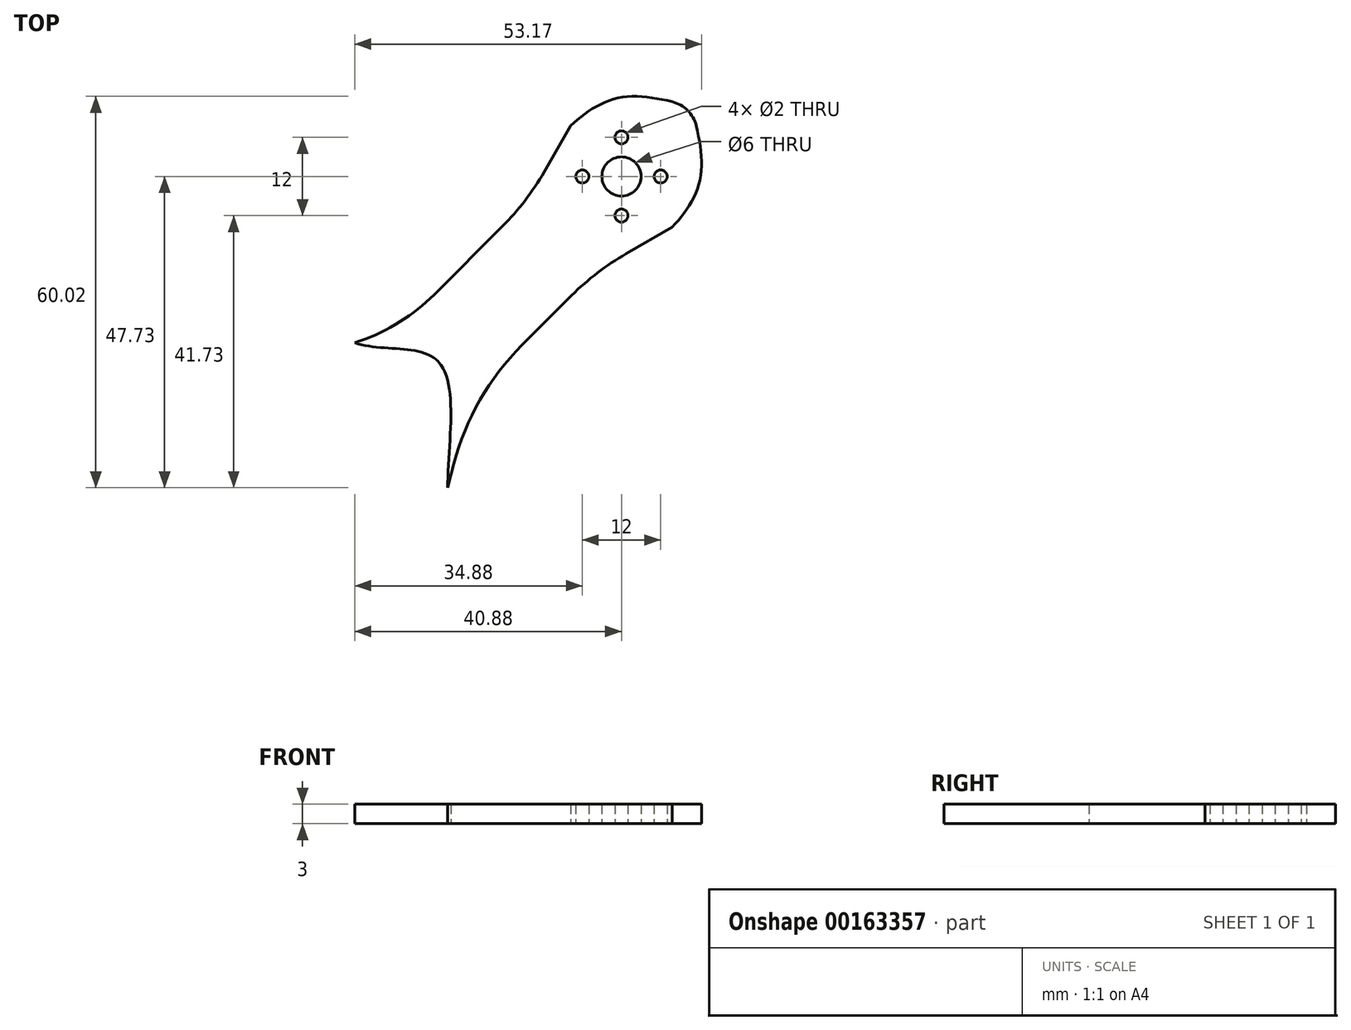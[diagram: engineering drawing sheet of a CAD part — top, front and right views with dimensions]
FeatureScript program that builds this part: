
annotation { "Feature Type Name" : "Feature", "Feature Type Description" : "" }
export const myFeature = defineFeature(function(context is Context, id is Id, definition is map)
    precondition{}
    {
        {
            var Q0;
            Q0=qCreatedBy(makeId("Top.planeOp"),FACE);
            var sketch = newSketch(context, id + "F0", { "sketchPlane" : qUnion([Q0])});
            skLineSegment(sketch, "E0.bottom", {"start": v(18, 18) * mm, "end": v(-18, 18) * mm, "construction": true});
            skLineSegment(sketch, "E0.top", {"start": v(18, -18) * mm, "end": v(-18, -18) * mm, "construction": true});
            skLineSegment(sketch, "E0.left", {"start": v(18, 18) * mm, "end": v(18, -18) * mm, "construction": true});
            skLineSegment(sketch, "E0.right", {"start": v(-18, 18) * mm, "end": v(-18, -18) * mm, "construction": true});
            skPoint(sketch, "E0.middle", {"position": v(0, 0) * mm});
            skLineSegment(sketch, "E1.bottom", {"start": v(15.25, 15.25) * mm, "end": v(-15.25, 15.25) * mm, "construction": true});
            skLineSegment(sketch, "E1.top", {"start": v(15.25, -15.25) * mm, "end": v(-15.25, -15.25) * mm, "construction": true});
            skLineSegment(sketch, "E1.left", {"start": v(15.25, 15.25) * mm, "end": v(15.25, -15.25) * mm, "construction": true});
            skLineSegment(sketch, "E1.right", {"start": v(-15.25, 15.25) * mm, "end": v(-15.25, -15.25) * mm, "construction": true});
            skCircle(sketch, "E2", {"center": v(15.25, 15.25) * mm, "radius": 1.5 * mm});
            skCircle(sketch, "E3", {"center": v(15.25, -15.25) * mm, "radius": 1.5 * mm});
            skCircle(sketch, "E4", {"center": v(-15.25, -15.25) * mm, "radius": 1.5 * mm});
            skCircle(sketch, "E5", {"center": v(-15.25, 15.25) * mm, "radius": 1.5 * mm});
            skLineSegment(sketch, "E6", {"start": v(-47.73, -47.73) * mm, "end": v(0, 0) * mm, "construction": true});
            skLineSegment(sketch, "E7", {"start": v(0, 0) * mm, "end": v(47.73, 47.73) * mm, "construction": true});
            skLineSegment(sketch, "E8", {"start": v(0, 44.74) * mm, "end": v(0, -45.9) * mm, "construction": true});
            skLineSegment(sketch, "E9", {"start": v(-44.2, 0) * mm, "end": v(46.03, 0) * mm, "construction": true});
            skLineSegment(sketch, "E10.MirrorCS", {"start": v(47.73, -47.73) * mm, "end": v(0, 0) * mm, "construction": true});
            skLineSegment(sketch, "E11.MirrorCS", {"start": v(0, 0) * mm, "end": v(-47.73, 47.73) * mm, "construction": true});
            skCircle(sketch, "E12", {"center": v(47.73, 47.73) * mm, "radius": 9 * mm, "construction": true});
            skCircle(sketch, "E13", {"center": v(47.73, 47.73) * mm, "radius": 6 * mm, "construction": true});
            skCircle(sketch, "E14", {"center": v(47.73, 47.73) * mm, "radius": 3 * mm});
            skLineSegment(sketch, "E15", {"start": v(47.73, 47.73) * mm, "end": v(47.73, 56.73) * mm, "construction": true});
            skLineSegment(sketch, "E16", {"start": v(47.73, 56.73) * mm, "end": v(47.73, 47.73) * mm, "construction": true});
            skLineSegment(sketch, "E17", {"start": v(47.73, 38.73) * mm, "end": v(47.73, 47.73) * mm, "construction": true});
            skLineSegment(sketch, "E18", {"start": v(47.73, 47.73) * mm, "end": v(56.73, 47.73) * mm, "construction": true});
            skLineSegment(sketch, "E19", {"start": v(38.73, 47.73) * mm, "end": v(47.73, 47.73) * mm, "construction": true});
            skCircle(sketch, "E20", {"center": v(47.73, 53.73) * mm, "radius": 1 * mm});
            skCircle(sketch, "E21", {"center": v(53.73, 47.73) * mm, "radius": 1 * mm});
            skCircle(sketch, "E22", {"center": v(47.73, 41.73) * mm, "radius": 1 * mm});
            skCircle(sketch, "E23", {"center": v(41.73, 47.73) * mm, "radius": 1 * mm});
            skCircle(sketch, "E24.MirrorC", {"center": v(-47.73, 47.73) * mm, "radius": 9 * mm, "construction": true});
            skCircle(sketch, "E25.MirrorC", {"center": v(-47.73, 47.73) * mm, "radius": 6 * mm, "construction": true});
            skCircle(sketch, "E26.MirrorC", {"center": v(-47.73, 41.73) * mm, "radius": 1 * mm, "construction": true});
            skCircle(sketch, "E27.MirrorC", {"center": v(-47.73, 41.73) * mm, "radius": 1 * mm});
            skLineSegment(sketch, "E28.MirrorCS", {"start": v(-47.73, 38.73) * mm, "end": v(-47.73, 47.73) * mm, "construction": true});
            skCircle(sketch, "E29.MirrorC", {"center": v(-47.73, 47.73) * mm, "radius": 3 * mm, "construction": true});
            skCircle(sketch, "E30.MirrorC", {"center": v(-47.73, 47.73) * mm, "radius": 3 * mm});
            skLineSegment(sketch, "E31.MirrorCS", {"start": v(-47.73, 47.73) * mm, "end": v(-56.73, 47.73) * mm, "construction": true});
            skCircle(sketch, "E32.MirrorC", {"center": v(-53.73, 47.73) * mm, "radius": 1 * mm, "construction": true});
            skCircle(sketch, "E33.MirrorC", {"center": v(-53.73, 47.73) * mm, "radius": 1 * mm});
            skCircle(sketch, "E34.MirrorC", {"center": v(-47.73, 53.73) * mm, "radius": 1 * mm, "construction": true});
            skCircle(sketch, "E35.MirrorC", {"center": v(-47.73, 53.73) * mm, "radius": 1 * mm});
            skLineSegment(sketch, "E36.MirrorCS", {"start": v(-47.73, 56.73) * mm, "end": v(-47.73, 47.73) * mm, "construction": true});
            skCircle(sketch, "E37.MirrorC", {"center": v(-41.73, 47.73) * mm, "radius": 1 * mm, "construction": true});
            skCircle(sketch, "E38.MirrorC", {"center": v(-41.73, 47.73) * mm, "radius": 1 * mm});
            skLineSegment(sketch, "E39.MirrorCS", {"start": v(-38.73, 47.73) * mm, "end": v(-47.73, 47.73) * mm, "construction": true});
            skCircle(sketch, "E40.MirrorC", {"center": v(47.73, -47.73) * mm, "radius": 9 * mm, "construction": true});
            skCircle(sketch, "E41.MirrorC", {"center": v(47.73, -47.73) * mm, "radius": 6 * mm, "construction": true});
            skCircle(sketch, "E42.MirrorC", {"center": v(53.73, -47.73) * mm, "radius": 1 * mm, "construction": true});
            skCircle(sketch, "E43.MirrorC", {"center": v(53.73, -47.73) * mm, "radius": 1 * mm});
            skLineSegment(sketch, "E44.MirrorCS", {"start": v(47.73, -47.73) * mm, "end": v(56.73, -47.73) * mm, "construction": true});
            skCircle(sketch, "E45.MirrorC", {"center": v(47.73, -47.73) * mm, "radius": 3 * mm, "construction": true});
            skCircle(sketch, "E46.MirrorC", {"center": v(47.73, -47.73) * mm, "radius": 3 * mm});
            skLineSegment(sketch, "E47.MirrorCS", {"start": v(47.73, -38.73) * mm, "end": v(47.73, -47.73) * mm, "construction": true});
            skLineSegment(sketch, "E48.MirrorCS", {"start": v(38.73, -47.73) * mm, "end": v(47.73, -47.73) * mm, "construction": true});
            skCircle(sketch, "E49.MirrorC", {"center": v(41.73, -47.73) * mm, "radius": 1 * mm, "construction": true});
            skCircle(sketch, "E50.MirrorC", {"center": v(41.73, -47.73) * mm, "radius": 1 * mm});
            skCircle(sketch, "E51.MirrorC", {"center": v(47.73, -53.73) * mm, "radius": 1 * mm, "construction": true});
            skCircle(sketch, "E52.MirrorC", {"center": v(47.73, -53.73) * mm, "radius": 1 * mm});
            skLineSegment(sketch, "E53.MirrorCS", {"start": v(47.73, -56.73) * mm, "end": v(47.73, -47.73) * mm, "construction": true});
            skCircle(sketch, "E54.MirrorC", {"center": v(47.73, -41.73) * mm, "radius": 1 * mm, "construction": true});
            skCircle(sketch, "E55.MirrorC", {"center": v(47.73, -41.73) * mm, "radius": 1 * mm});
            skCircle(sketch, "E56.MirrorC", {"center": v(-47.73, -47.73) * mm, "radius": 9 * mm, "construction": true});
            skCircle(sketch, "E57.MirrorC", {"center": v(-41.73, -47.73) * mm, "radius": 1 * mm, "construction": true});
            skCircle(sketch, "E58.MirrorC", {"center": v(-41.73, -47.73) * mm, "radius": 1 * mm});
            skLineSegment(sketch, "E59.MirrorCS", {"start": v(-38.73, -47.73) * mm, "end": v(-47.73, -47.73) * mm, "construction": true});
            skCircle(sketch, "E60.MirrorC", {"center": v(-47.73, -47.73) * mm, "radius": 6 * mm, "construction": true});
            skCircle(sketch, "E61.MirrorC", {"center": v(-47.73, -41.73) * mm, "radius": 1 * mm, "construction": true});
            skCircle(sketch, "E62.MirrorC", {"center": v(-47.73, -41.73) * mm, "radius": 1 * mm});
            skLineSegment(sketch, "E63.MirrorCS", {"start": v(-47.73, -47.73) * mm, "end": v(-56.73, -47.73) * mm, "construction": true});
            skCircle(sketch, "E64.MirrorC", {"center": v(-53.73, -47.73) * mm, "radius": 1 * mm, "construction": true});
            skCircle(sketch, "E65.MirrorC", {"center": v(-53.73, -47.73) * mm, "radius": 1 * mm});
            skCircle(sketch, "E66.MirrorC", {"center": v(-47.73, -53.73) * mm, "radius": 1 * mm, "construction": true});
            skCircle(sketch, "E67.MirrorC", {"center": v(-47.73, -53.73) * mm, "radius": 1 * mm});
            skLineSegment(sketch, "E68.MirrorCS", {"start": v(-47.73, -56.73) * mm, "end": v(-47.73, -47.73) * mm, "construction": true});
            skLineSegment(sketch, "E69.MirrorCS", {"start": v(-47.73, -38.73) * mm, "end": v(-47.73, -47.73) * mm, "construction": true});
            skLineSegment(sketch, "E70.bottom", {"start": v(19.5, 19.5) * mm, "end": v(-19.5, 19.5) * mm, "construction": true});
            skLineSegment(sketch, "E70.top", {"start": v(19.5, -19.5) * mm, "end": v(-19.5, -19.5) * mm, "construction": true});
            skLineSegment(sketch, "E70.left", {"start": v(19.5, 19.5) * mm, "end": v(19.5, -19.5) * mm, "construction": true});
            skLineSegment(sketch, "E70.right", {"start": v(-19.5, 19.5) * mm, "end": v(-19.5, -19.5) * mm, "construction": true});
            skFitSpline(sketch, "E71", {"points": [v(-19.5, 19.5) * mm, v(-6.87, 22.22) * mm, v(0, 25.99) * mm, v(6.85, 22.22) * mm, v(19.5, 19.5) * mm, v(21.07, 0) * mm, v(19.5, -19.5) * mm, v(0, -34) * mm, v(-19.5, -19.5) * mm, v(-21.07, 0) * mm, v(-19.5, 19.5) * mm]});
            skCircle(sketch, "E72.cCircle", {"center": v(0, 22.21) * mm, "radius": 2.75 * mm, "construction": true});
            skLineSegment(sketch, "E72.0", {"start": v(2.68, 22.82) * mm, "end": v(1.87, 20.2) * mm, "construction": true});
            skLineSegment(sketch, "E72.1", {"start": v(1.87, 20.2) * mm, "end": v(-0.81, 19.58) * mm, "construction": true});
            skLineSegment(sketch, "E72.2", {"start": v(-0.81, 19.58) * mm, "end": v(-2.68, 21.6) * mm, "construction": true});
            skLineSegment(sketch, "E72.3", {"start": v(-2.68, 21.6) * mm, "end": v(-1.87, 24.23) * mm, "construction": true});
            skLineSegment(sketch, "E72.4", {"start": v(-1.87, 24.23) * mm, "end": v(0.81, 24.84) * mm, "construction": true});
            skLineSegment(sketch, "E72.5", {"start": v(0.81, 24.84) * mm, "end": v(2.68, 22.82) * mm, "construction": true});
            skCircle(sketch, "E73.cCircle", {"center": v(0, -30.03) * mm, "radius": 2.75 * mm, "construction": true});
            skLineSegment(sketch, "E73.0", {"start": v(2.68, -29.42) * mm, "end": v(1.87, -32.05) * mm, "construction": true});
            skLineSegment(sketch, "E73.1", {"start": v(1.87, -32.05) * mm, "end": v(-0.81, -32.65) * mm, "construction": true});
            skLineSegment(sketch, "E73.2", {"start": v(-0.81, -32.65) * mm, "end": v(-2.68, -30.63) * mm, "construction": true});
            skLineSegment(sketch, "E73.3", {"start": v(-2.68, -30.63) * mm, "end": v(-1.87, -28) * mm, "construction": true});
            skLineSegment(sketch, "E73.4", {"start": v(-1.87, -28) * mm, "end": v(0.81, -27.4) * mm, "construction": true});
            skLineSegment(sketch, "E73.5", {"start": v(0.81, -27.4) * mm, "end": v(2.68, -29.42) * mm, "construction": true});
            skPoint(sketch, "E74", {"position": v(0, 19.5) * mm});
            skLineSegment(sketch, "E75", {"start": v(-6.87, 22.22) * mm, "end": v(6.85, 22.22) * mm, "construction": true});
            skLineSegment(sketch, "E76", {"start": v(55.5, 39.95) * mm, "end": v(55.5, 39.95) * mm});
            skLineSegment(sketch, "E77", {"start": v(33.23, 43.84) * mm, "end": v(38.54, 38.54) * mm, "construction": true});
            skLineSegment(sketch, "E78", {"start": v(38.54, 38.54) * mm, "end": v(43.84, 33.23) * mm, "construction": true});
            skLineSegment(sketch, "E79", {"start": v(39.95, 55.5) * mm, "end": v(47.73, 47.73) * mm, "construction": true});
            skLineSegment(sketch, "E80", {"start": v(47.73, 47.73) * mm, "end": v(55.5, 39.95) * mm, "construction": true});
            skLineSegment(sketch, "E81", {"start": v(39.95, 55.5) * mm, "end": v(35.87, 48.43) * mm});
            skLineSegment(sketch, "E82", {"start": v(55.5, 39.95) * mm, "end": v(48.43, 35.87) * mm});
            skLineSegment(sketch, "E83", {"start": v(14.2, 24.8) * mm, "end": v(19.5, 19.5) * mm, "construction": true});
            skLineSegment(sketch, "E84", {"start": v(19.5, 19.5) * mm, "end": v(24.8, 14.2) * mm, "construction": true});
            skLineSegment(sketch, "E85", {"start": v(29.5, 40.1) * mm, "end": v(19.03, 29.64) * mm});
            skLineSegment(sketch, "E86", {"start": v(40.1, 29.5) * mm, "end": v(32.46, 21.85) * mm});
            skLineSegment(sketch, "E87", {"start": v(22.05, 3.73) * mm, "end": v(21.07, 0) * mm});
            skLineSegment(sketch, "E88", {"start": v(7.75, 22.54) * mm, "end": v(6.85, 22.22) * mm});
            skPoint(sketch, "E89.visualSharp", {"position": v(24.8, 14.2) * mm});
            skArc(sketch, "E89.filletArc", {"start": v(32.46, 21.85) * mm, "mid": v(26.05, 13.48) * mm, "end": v(22.05, 3.73) * mm});
            skPoint(sketch, "E90.visualSharp", {"position": v(14.2, 24.8) * mm});
            skArc(sketch, "E90.filletArc", {"start": v(7.75, 22.54) * mm, "mid": v(13.79, 25.45) * mm, "end": v(19.03, 29.64) * mm});
            skPoint(sketch, "E91.visualSharp", {"position": v(33.23, 43.84) * mm});
            skArc(sketch, "E91.filletArc", {"start": v(29.5, 40.1) * mm, "mid": v(32.96, 44.05) * mm, "end": v(35.87, 48.43) * mm});
            skPoint(sketch, "E92.visualSharp", {"position": v(43.84, 33.23) * mm});
            skArc(sketch, "E92.filletArc", {"start": v(48.43, 35.87) * mm, "mid": v(44.05, 32.96) * mm, "end": v(40.1, 29.5) * mm});
            skLineSegment(sketch, "E93.MirrorCS", {"start": v(-7.75, 22.54) * mm, "end": v(-6.85, 22.22) * mm});
            skArc(sketch, "E94.MirrorCS", {"start": v(-7.75, 22.54) * mm, "mid": v(-13.79, 25.45) * mm, "end": v(-19.03, 29.64) * mm});
            skLineSegment(sketch, "E95.MirrorCS", {"start": v(-29.5, 40.1) * mm, "end": v(-19.03, 29.64) * mm});
            skArc(sketch, "E96.MirrorCS", {"start": v(-29.5, 40.1) * mm, "mid": v(-32.96, 44.05) * mm, "end": v(-35.87, 48.43) * mm});
            skLineSegment(sketch, "E97.MirrorCS", {"start": v(-39.95, 55.5) * mm, "end": v(-35.87, 48.43) * mm});
            skLineSegment(sketch, "E98.MirrorCS", {"start": v(-55.5, 39.95) * mm, "end": v(-55.5, 39.95) * mm});
            skLineSegment(sketch, "E99.MirrorCS", {"start": v(-55.5, 39.95) * mm, "end": v(-48.43, 35.87) * mm});
            skArc(sketch, "E100.MirrorCS", {"start": v(-48.43, 35.87) * mm, "mid": v(-44.05, 32.96) * mm, "end": v(-40.1, 29.5) * mm});
            skLineSegment(sketch, "E101.MirrorCS", {"start": v(-40.1, 29.5) * mm, "end": v(-32.46, 21.85) * mm});
            skArc(sketch, "E102.MirrorCS", {"start": v(-32.46, 21.85) * mm, "mid": v(-26.05, 13.48) * mm, "end": v(-22.05, 3.73) * mm});
            skLineSegment(sketch, "E103.MirrorCS", {"start": v(-22.05, 3.73) * mm, "end": v(-21.07, 0) * mm});
            skLineSegment(sketch, "E104.MirrorCS", {"start": v(14.2, -24.8) * mm, "end": v(19.5, -19.5) * mm, "construction": true});
            skLineSegment(sketch, "E105.MirrorCS", {"start": v(19.5, -19.5) * mm, "end": v(24.8, -14.2) * mm, "construction": true});
            skLineSegment(sketch, "E106.MirrorCS", {"start": v(33.23, -43.84) * mm, "end": v(38.54, -38.54) * mm, "construction": true});
            skLineSegment(sketch, "E107.MirrorCS", {"start": v(38.54, -38.54) * mm, "end": v(43.84, -33.23) * mm, "construction": true});
            skLineSegment(sketch, "E108.MirrorCS", {"start": v(55.5, -39.95) * mm, "end": v(55.5, -39.95) * mm});
            skLineSegment(sketch, "E109.MirrorCS", {"start": v(55.5, -39.95) * mm, "end": v(48.43, -35.87) * mm});
            skLineSegment(sketch, "E110.MirrorCS", {"start": v(39.95, -55.5) * mm, "end": v(35.87, -48.43) * mm});
            skArc(sketch, "E111.MirrorCS", {"start": v(48.43, -35.87) * mm, "mid": v(44.05, -32.96) * mm, "end": v(40.1, -29.5) * mm});
            skArc(sketch, "E112.MirrorCS", {"start": v(29.5, -40.1) * mm, "mid": v(32.96, -44.05) * mm, "end": v(35.87, -48.43) * mm});
            skLineSegment(sketch, "E113", {"start": v(40.1, -29.5) * mm, "end": v(32.46, -21.85) * mm});
            skLineSegment(sketch, "E114", {"start": v(22.05, -3.73) * mm, "end": v(21.07, 0) * mm});
            skLineSegment(sketch, "E115", {"start": v(29.5, -40.1) * mm, "end": v(20.34, -30.95) * mm});
            skPoint(sketch, "E116", {"position": v(0, -19.5) * mm});
            skPoint(sketch, "E117.visualSharp", {"position": v(14.2, -24.8) * mm});
            skArc(sketch, "E117.filletArc", {"start": v(20.34, -30.95) * mm, "mid": v(17.71, -28.54) * mm, "end": v(14.88, -26.38) * mm});
            skPoint(sketch, "E118.visualSharp", {"position": v(24.8, -14.2) * mm});
            skArc(sketch, "E118.filletArc", {"start": v(22.05, -3.73) * mm, "mid": v(26.05, -13.48) * mm, "end": v(32.46, -21.85) * mm});
            skArc(sketch, "E119.MirrorCS", {"start": v(-20.34, -30.95) * mm, "mid": v(-17.71, -28.54) * mm, "end": v(-14.88, -26.38) * mm});
            skLineSegment(sketch, "E120.MirrorCS", {"start": v(-29.5, -40.1) * mm, "end": v(-20.34, -30.95) * mm});
            skArc(sketch, "E121.MirrorCS", {"start": v(-29.5, -40.1) * mm, "mid": v(-32.96, -44.05) * mm, "end": v(-35.87, -48.43) * mm});
            skLineSegment(sketch, "E122.MirrorCS", {"start": v(-39.95, -55.5) * mm, "end": v(-35.87, -48.43) * mm});
            skArc(sketch, "E123.MirrorCS", {"start": v(-55.5, -39.95) * mm, "mid": v(-55.9, -40.36) * mm, "end": v(-56.26, -40.8) * mm});
            skLineSegment(sketch, "E124.MirrorCS", {"start": v(-55.5, -39.95) * mm, "end": v(-48.43, -35.87) * mm});
            skArc(sketch, "E125.MirrorCS", {"start": v(-48.43, -35.87) * mm, "mid": v(-44.05, -32.96) * mm, "end": v(-40.1, -29.5) * mm});
            skLineSegment(sketch, "E126.MirrorCS", {"start": v(-40.1, -29.5) * mm, "end": v(-32.46, -21.85) * mm});
            skArc(sketch, "E127.MirrorCS", {"start": v(-22.05, -3.73) * mm, "mid": v(-26.05, -13.48) * mm, "end": v(-32.46, -21.85) * mm});
            skLineSegment(sketch, "E128.MirrorCS", {"start": v(-22.05, -3.73) * mm, "end": v(-21.07, 0) * mm});
            skFitSpline(sketch, "E129.trimOffspring", {"points": [v(-19.5, 19.5) * mm, v(-6.87, 22.22) * mm, v(0, 26) * mm, v(6.85, 22.22) * mm, v(19.5, 19.5) * mm, v(21.07, 0) * mm, v(19.5, -19.5) * mm, v(0, -34) * mm, v(-19.5, -19.5) * mm, v(-21.07, 0) * mm, v(-19.5, 19.5) * mm]});
            skPoint(sketch, "E130.orphan", {"position": v(-6.06, -21.76) * mm});
            skPoint(sketch, "E131.orphan", {"position": v(6.06, -21.76) * mm});
            skFitSpline(sketch, "E132.trimOffspring", {"points": [v(-19.5, 19.5) * mm, v(-6.87, 22.22) * mm, v(0, 26) * mm, v(6.85, 22.22) * mm, v(19.5, 19.5) * mm, v(21.07, 0) * mm, v(19.5, -19.5) * mm, v(0, -34) * mm, v(-19.5, -19.5) * mm, v(-21.07, 0) * mm, v(-19.5, 19.5) * mm]});
            skCircle(sketch, "E133.MirrorC", {"center": v(-47.73, -47.73) * mm, "radius": 3 * mm});
            skLineSegment(sketch, "E134.bottom", {"start": v(10.5, 10) * mm, "end": v(13.5, 10) * mm});
            skLineSegment(sketch, "E134.top", {"start": v(10.5, -10) * mm, "end": v(13.5, -10) * mm});
            skLineSegment(sketch, "E134.left", {"start": v(10.5, 10) * mm, "end": v(10.5, -10) * mm});
            skLineSegment(sketch, "E134.right", {"start": v(13.5, 10) * mm, "end": v(13.5, -10) * mm});
            skPoint(sketch, "E134.middle", {"position": v(12, 0) * mm});
            skLineSegment(sketch, "E135.MirrorCS", {"start": v(-10.5, 10) * mm, "end": v(-13.5, 10) * mm});
            skLineSegment(sketch, "E136.MirrorCS", {"start": v(-13.5, 10) * mm, "end": v(-13.5, -10) * mm});
            skLineSegment(sketch, "E137.MirrorCS", {"start": v(-10.5, 10) * mm, "end": v(-10.5, -10) * mm});
            skLineSegment(sketch, "E138.MirrorCS", {"start": v(-10.5, -10) * mm, "end": v(-13.5, -10) * mm});
            skCircle(sketch, "E139", {"center": v(0, 22.21) * mm, "radius": 1.5 * mm});
            skCircle(sketch, "E140", {"center": v(0, -30.03) * mm, "radius": 1.5 * mm});
            skLineSegment(sketch, "E141", {"start": v(47.73, 47.73) * mm, "end": v(58.43, 58.43) * mm, "construction": true});
            skLineSegment(sketch, "E142", {"start": v(47.73, 56.73) * mm, "end": v(47.73, 59.86) * mm, "construction": true});
            skFitSpline(sketch, "E143", {"points": [v(39.95, 55.5) * mm, v(47.73, 59.86) * mm, v(58.43, 58.43) * mm, v(67.08, 55.96) * mm], "startDerivative": vector(19.86, 18.67) * mm, "endDerivative": vector(24.91, -8.05) * mm});
            skLineSegment(sketch, "E144.trimOffspring", {"start": v(39.95, 55.5) * mm, "end": v(39.95, 55.5) * mm});
            skFitSpline(sketch, "E145.MirrorCS", {"points": [v(55.5, 39.95) * mm, v(59.86, 47.73) * mm, v(58.43, 58.43) * mm, v(55.96, 67.08) * mm], "startDerivative": vector(18.67, 19.86) * mm, "endDerivative": vector(-8.05, 24.91) * mm});
            skFitSpline(sketch, "E146.MirrorCS", {"points": [v(-39.95, 55.5) * mm, v(-47.73, 59.86) * mm, v(-58.43, 58.43) * mm, v(-67.08, 55.96) * mm], "startDerivative": vector(-19.86, 18.67) * mm, "endDerivative": vector(-24.91, -8.05) * mm});
            skFitSpline(sketch, "E147.MirrorCS", {"points": [v(-55.5, 39.95) * mm, v(-59.86, 47.73) * mm, v(-58.43, 58.43) * mm, v(-55.96, 67.08) * mm], "startDerivative": vector(-18.67, 19.86) * mm, "endDerivative": vector(8.05, 24.91) * mm});
            skFitSpline(sketch, "E148.MirrorCS", {"points": [v(39.95, -55.5) * mm, v(47.73, -59.86) * mm, v(58.43, -58.43) * mm, v(67.08, -55.96) * mm], "startDerivative": vector(19.86, -18.67) * mm, "endDerivative": vector(24.91, 8.05) * mm});
            skFitSpline(sketch, "E149.MirrorCS", {"points": [v(55.5, -39.95) * mm, v(59.86, -47.73) * mm, v(58.43, -58.43) * mm, v(55.96, -67.08) * mm], "startDerivative": vector(18.67, -19.86) * mm, "endDerivative": vector(-8.05, -24.91) * mm});
            skFitSpline(sketch, "E150.MirrorCS", {"points": [v(-55.5, -39.95) * mm, v(-59.86, -47.73) * mm, v(-58.43, -58.43) * mm, v(-55.96, -67.08) * mm], "startDerivative": vector(-18.67, -19.86) * mm, "endDerivative": vector(8.05, -24.91) * mm});
            skFitSpline(sketch, "E151.MirrorCS", {"points": [v(-39.95, -55.5) * mm, v(-47.73, -59.86) * mm, v(-58.43, -58.43) * mm, v(-67.08, -55.96) * mm], "startDerivative": vector(-19.86, -18.67) * mm, "endDerivative": vector(-24.91, 8.05) * mm});
            skLineSegment(sketch, "E152.trimOffspring", {"start": v(39.95, -55.5) * mm, "end": v(39.95, -55.5) * mm});
            skArc(sketch, "E153.trimOffspring", {"start": v(-40.8, -56.27) * mm, "mid": v(-40.36, -55.9) * mm, "end": v(-39.95, -55.5) * mm});
            skLineSegment(sketch, "E154.trimOffspring", {"start": v(-39.95, 55.5) * mm, "end": v(-39.95, 55.5) * mm});
            skArc(sketch, "E155.filletArc", {"start": v(59.19, 55.5) * mm, "mid": v(57.86, 57.86) * mm, "end": v(55.5, 59.19) * mm});
            skArc(sketch, "E156.filletArc", {"start": v(-55.5, 59.19) * mm, "mid": v(-57.86, 57.86) * mm, "end": v(-59.19, 55.5) * mm});
            skArc(sketch, "E157.filletArc", {"start": v(55.5, -59.19) * mm, "mid": v(57.86, -57.86) * mm, "end": v(59.19, -55.5) * mm});
            skArc(sketch, "E158.filletArc", {"start": v(-59.19, -55.5) * mm, "mid": v(-57.86, -57.86) * mm, "end": v(-55.5, -59.19) * mm});
            skLineSegment(sketch, "E159", {"start": v(0, -22.36) * mm, "end": v(3, -22.36) * mm, "construction": true});
            skLineSegment(sketch, "E160.left", {"start": v(3.77, -23.88) * mm, "end": v(3.77, -20.88) * mm});
            skLineSegment(sketch, "E160.right", {"start": v(2.23, -23.85) * mm, "end": v(2.23, -20.85) * mm});
            skPoint(sketch, "E160.middle", {"position": v(3, -22.36) * mm});
            skLineSegment(sketch, "E161.MirrorCS", {"start": v(-2.23, -23.85) * mm, "end": v(-2.23, -20.85) * mm});
            skLineSegment(sketch, "E162.MirrorCS", {"start": v(-3.77, -23.88) * mm, "end": v(-3.77, -20.88) * mm});
            skArc(sketch, "E163", {"start": v(2.23, -20.85) * mm, "mid": v(3.01, -20.08) * mm, "end": v(3.77, -20.88) * mm});
            skPoint(sketch, "E164.MirrorCS.end.orphan", {"position": v(-2.23, -23.85) * mm});
            skPoint(sketch, "E164.MirrorCS.start.orphan", {"position": v(-3.77, -23.88) * mm});
            skPoint(sketch, "E165.MirrorCS.end.orphan", {"position": v(-2.23, -20.85) * mm});
            skPoint(sketch, "E165.MirrorCS.start.orphan", {"position": v(-3.77, -20.88) * mm});
            skArc(sketch, "E166", {"start": v(2.23, -23.85) * mm, "mid": v(2.99, -24.62) * mm, "end": v(3.77, -23.88) * mm});
            skArc(sketch, "E167.MirrorCS", {"start": v(-2.23, -20.85) * mm, "mid": v(-3.01, -20.08) * mm, "end": v(-3.77, -20.88) * mm});
            skArc(sketch, "E168.MirrorCS", {"start": v(-2.23, -23.85) * mm, "mid": v(-2.99, -24.62) * mm, "end": v(-3.77, -23.88) * mm});
            skSolve(sketch);
        }
        {
            var Q0;
            Q0=qCreatedBy(makeId("Top.planeOp"),FACE);
            cPlane(context, id + "F1", {"entities" : qUnion([Q0]), "cplaneType" : CPlaneType.OFFSET, "offset" : 15 * mm, "width" : 150 * mm, "height" : 150 * mm});
        }
        {
            var Q0;
            Q0=qCreatedBy(id+"F1.planeOp",FACE);
            var sketch = newSketch(context, id + "F2", { "sketchPlane" : qUnion([Q0])});
            skLineSegment(sketch, "E169.bottom", {"start": v(17.96, 18.03) * mm, "end": v(-18.04, 18.03) * mm, "construction": true});
            skLineSegment(sketch, "E169.top", {"start": v(17.96, -17.97) * mm, "end": v(-18.04, -17.97) * mm, "construction": true});
            skLineSegment(sketch, "E169.left", {"start": v(17.96, 18.03) * mm, "end": v(17.96, -17.97) * mm, "construction": true});
            skLineSegment(sketch, "E169.right", {"start": v(-18.04, 18.03) * mm, "end": v(-18.04, -17.97) * mm, "construction": true});
            skPoint(sketch, "E169.middle", {"position": v(-0.04, 0.03) * mm});
            skLineSegment(sketch, "E170.bottom", {"start": v(15.2, 15.28) * mm, "end": v(-15.3, 15.28) * mm, "construction": true});
            skLineSegment(sketch, "E170.top", {"start": v(15.2, -15.22) * mm, "end": v(-15.3, -15.22) * mm, "construction": true});
            skLineSegment(sketch, "E170.left", {"start": v(15.2, 15.28) * mm, "end": v(15.2, -15.22) * mm, "construction": true});
            skLineSegment(sketch, "E170.right", {"start": v(-15.3, 15.28) * mm, "end": v(-15.3, -15.22) * mm, "construction": true});
            skCircle(sketch, "E171", {"center": v(15.2, 15.28) * mm, "radius": 1.5 * mm});
            skCircle(sketch, "E172", {"center": v(15.2, -15.22) * mm, "radius": 1.5 * mm});
            skCircle(sketch, "E173", {"center": v(-15.3, -15.22) * mm, "radius": 1.5 * mm});
            skCircle(sketch, "E174", {"center": v(-15.3, 15.28) * mm, "radius": 1.5 * mm});
            skLineSegment(sketch, "E175", {"start": v(-0.04, 44.77) * mm, "end": v(-0.04, -45.88) * mm, "construction": true});
            skLineSegment(sketch, "E176", {"start": v(-44.25, 0.03) * mm, "end": v(46, 0.03) * mm, "construction": true});
            skSolve(sketch);
        }
        {
            var Q0;
            Q0=qCreatedBy(makeId("Top.planeOp"),FACE);
            cPlane(context, id + "F3", {"entities" : qUnion([Q0]), "cplaneType" : CPlaneType.OFFSET, "offset" : 27 * mm, "width" : 150 * mm, "height" : 150 * mm});
        }
        {
            var Q0;
            Q0=qCreatedBy(makeId("Right.planeOp"),FACE);
            var sketch = newSketch(context, id + "F4", { "sketchPlane" : qUnion([Q0])});
            skLineSegment(sketch, "E177", {"start": v(1.3, 0) * mm, "end": v(1.3, 25) * mm, "construction": true});
            skLineSegment(sketch, "E178", {"start": v(1.3, 25) * mm, "end": v(-5.2, 36.26) * mm, "construction": true});
            skLineSegment(sketch, "E179", {"start": v(-5.2, 36.26) * mm, "end": v(5.2, 42.26) * mm, "construction": true});
            skLineSegment(sketch, "E180", {"start": v(5.2, 42.26) * mm, "end": v(18.2, 19.74) * mm, "construction": true});
            skLineSegment(sketch, "E181", {"start": v(18.2, 19.74) * mm, "end": v(7.8, 13.74) * mm, "construction": true});
            skLineSegment(sketch, "E182", {"start": v(7.8, 13.74) * mm, "end": v(1.3, 25) * mm, "construction": true});
            skLineSegment(sketch, "E183", {"start": v(5.2, 42.26) * mm, "end": v(22.17, 46.86) * mm, "construction": true});
            skLineSegment(sketch, "E184", {"start": v(22.17, 46.86) * mm, "end": v(30.67, 32.14) * mm, "construction": true});
            skLineSegment(sketch, "E185", {"start": v(30.67, 32.14) * mm, "end": v(18.2, 19.74) * mm, "construction": true});
            skLineSegment(sketch, "E186", {"start": v(1.3, 25) * mm, "end": v(26.42, 39.5) * mm, "construction": true});
            skLineSegment(sketch, "E187", {"start": v(18.2, 3.74) * mm, "end": v(4.77, 27) * mm, "construction": true});
            skLineSegment(sketch, "E188", {"start": v(4.77, 27) * mm, "end": v(3.2, 29.72) * mm, "construction": true});
            skSolve(sketch);
        }
        {
            var Q0;
            Q0=sQuery(id+"F4.wireOp",EDGE,"E184");
            var Q1;
            Q1=qCreatedBy(makeId("Top.planeOp"),FACE);
            cPlane(context, id + "F5", {"entities" : qUnion([Q0, Q1]), "cplaneType" : CPlaneType.LINE_ANGLE, "offset" : 25.4 * mm, "angle" : 0 * degree, "width" : 152.4 * mm, "height" : 152.4 * mm});
        }
        {
            var Q0;
            Q0=qCreatedBy(id+"F5.planeOp",FACE);
            cPlane(context, id + "F6", {"entities" : qUnion([Q0]), "cplaneType" : CPlaneType.OFFSET, "offset" : 0 * mm, "width" : 152.4 * mm, "height" : 152.4 * mm});
        }
        {
            var Q0;
            Q0=sQuery(id+"F0.wireOp",VERTEX,"E70.left.end");
            var Q1;
            Q1=sQuery(id+"F0.wireOp",EDGE,"E10.MirrorCS");
            cPlane(context, id + "F7", {"entities" : qUnion([Q0, Q1]), "cplaneType" : CPlaneType.LINE_POINT, "offset" : 25 * mm, "width" : 150 * mm, "height" : 150 * mm});
        }
        {
            var Q0;
            Q0=sQuery(id+"F0.wireOp",VERTEX,"E70.right.end");
            var Q1;
            Q1=sQuery(id+"F0.wireOp",EDGE,"E6");
            cPlane(context, id + "F8", {"entities" : qUnion([Q0, Q1]), "cplaneType" : CPlaneType.LINE_POINT, "offset" : 25 * mm, "width" : 150 * mm, "height" : 150 * mm});
        }
        {
            var Q0;
            Q0=sQuery(id+"F0.wireOp",VERTEX,"E70.right.start");
            var Q1;
            Q1=sQuery(id+"F0.wireOp",EDGE,"E11.MirrorCS");
            cPlane(context, id + "F9", {"entities" : qUnion([Q0, Q1]), "cplaneType" : CPlaneType.LINE_POINT, "offset" : 25 * mm, "width" : 150 * mm, "height" : 150 * mm});
        }
        {
            var Q0;
            Q0=sQuery(id+"F0.wireOp",VERTEX,"E70.left.start");
            var Q1;
            Q1=sQuery(id+"F0.wireOp",EDGE,"E7");
            cPlane(context, id + "F10", {"entities" : qUnion([Q0, Q1]), "cplaneType" : CPlaneType.LINE_POINT, "offset" : 25 * mm, "width" : 150 * mm, "height" : 150 * mm});
        }
        {
            var Q0;
            Q0=sQuery(id+"F0.wireOp",EDGE,"E9");
            var Q1;
            Q1=qCreatedBy(id+"F6.planeOp",FACE);
            cPlane(context, id + "F11", {"entities" : qUnion([Q0, Q1]), "cplaneType" : CPlaneType.LINE_ANGLE, "offset" : 25 * mm, "angle" : 90 * degree, "flipAlignment" : true, "width" : 150 * mm, "height" : 150 * mm});
        }
        {
            var Q0;
            Q0=makeQuery(id+"F0.imprint","IMPRINT",FACE,{"disambiguationData":[TD([[makeQuery(id+"F0.imprint","IMPRINT",EDGE,{"derivedFrom":sQuery(id+"F0.wireOp",EDGE,"E14")}),-1.0]])]});
            extrude(context, id + "F12", {"entities" : qUnion([Q0]), "depth" : 3 * mm});
        }
    });
